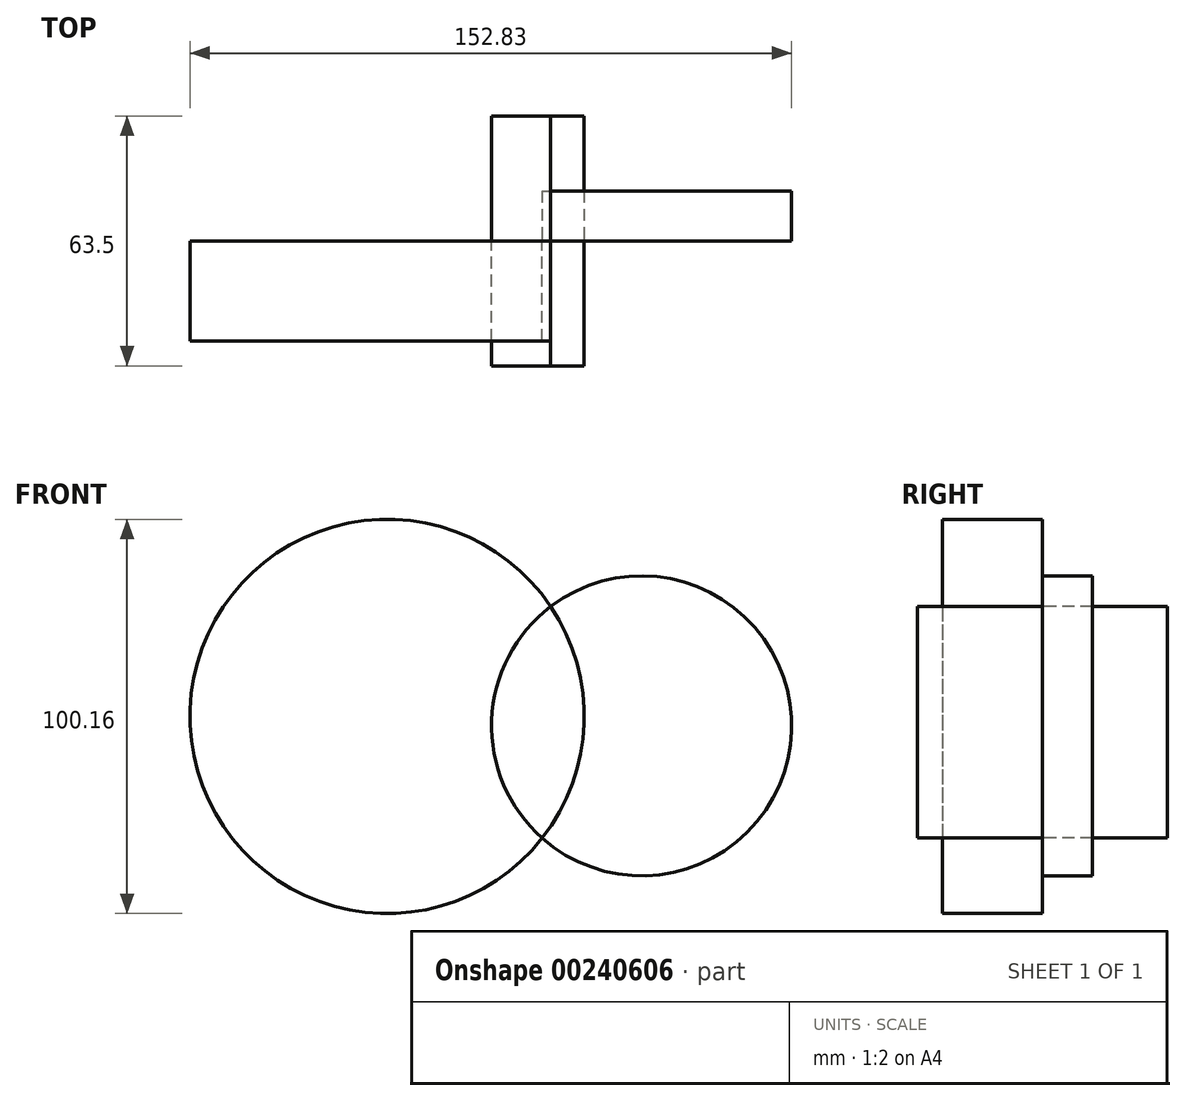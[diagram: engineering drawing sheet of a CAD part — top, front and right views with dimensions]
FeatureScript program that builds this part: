
annotation { "Feature Type Name" : "Feature", "Feature Type Description" : "" }
export const myFeature = defineFeature(function(context is Context, id is Id, definition is map)
    precondition{}
    {
        {
            var Q0;
            Q0=qCreatedBy(makeId("Front.planeOp"),FACE);
            var sketch = newSketch(context, id + "F0", { "sketchPlane" : qUnion([Q0])});
            skCircle(sketch, "E0", {"center": v(0, 0) * mm, "radius": 38.1 * mm});
            skCircle(sketch, "E1", {"center": v(-64.65, 2.38) * mm, "radius": 50.08 * mm});
            skPoint(sketch, "E1.first.point", {"position": v(-55.08, 51.54) * mm});
            skPoint(sketch, "E1.second.point", {"position": v(-16.98, 17.74) * mm});
            skPoint(sketch, "E1.third.point", {"position": v(-29.96, -33.73) * mm});
            skSolve(sketch);
        }
        {
            var Q0;
            {var subQ0=sQuery(id+"F0.wireOp",EDGE,"E1");var subQ1=sQuery(id+"F0.wireOp",EDGE,"E0");var subQ2=makeQuery(id+"F0.imprint","INTERSECT",VERTEX,{"disambiguationData":[OD(0.0)],"derivedFrom":[subQ1,subQ0]});Q0=makeQuery(id+"F0.imprint","IMPRINT",FACE,{"disambiguationData":[TD([[makeQuery(id+"F0.imprint","IMPRINT",EDGE,{"disambiguationData":[TD([[subQ2,1.0]])],"derivedFrom":subQ1}),-1.0]])]});}
            extrude(context, id + "F1", {"entities" : qUnion([Q0]), "depth" : 25.4 * mm});
        }
        {
            var Q0;
            {var subQ0=sQuery(id+"F0.wireOp",EDGE,"E1");var subQ1=sQuery(id+"F0.wireOp",EDGE,"E0");var subQ2=makeQuery(id+"F0.imprint","INTERSECT",VERTEX,{"disambiguationData":[OD(0.0)],"derivedFrom":[subQ1,subQ0]});Q0=makeQuery(id+"F0.imprint","IMPRINT",FACE,{"disambiguationData":[TD([[makeQuery(id+"F0.imprint","IMPRINT",EDGE,{"disambiguationData":[TD([[subQ2,-1.0]])],"derivedFrom":subQ1}),1.0]])]});}
            extrude(context, id + "F2", {"entities" : qUnion([Q0]), "oppositeDirection" : true, "depth" : 12.7 * mm});
        }
        {
            var Q0;
            {var subQ0=sQuery(id+"F0.wireOp",EDGE,"E1");var subQ1=sQuery(id+"F0.wireOp",EDGE,"E0");var subQ2=makeQuery(id+"F0.imprint","INTERSECT",VERTEX,{"disambiguationData":[OD(0.0)],"derivedFrom":[subQ1,subQ0]});Q0=makeQuery(id+"F0.imprint","IMPRINT",FACE,{"disambiguationData":[TD([[makeQuery(id+"F0.imprint","IMPRINT",EDGE,{"disambiguationData":[TD([[subQ2,1.0]])],"derivedFrom":subQ1}),1.0]])]});}
            extrude(context, id + "F3", {"entities" : qUnion([Q0]), "endBound" : BoundingType.SYMMETRIC, "depth" : 63.5 * mm});
        }
    });
